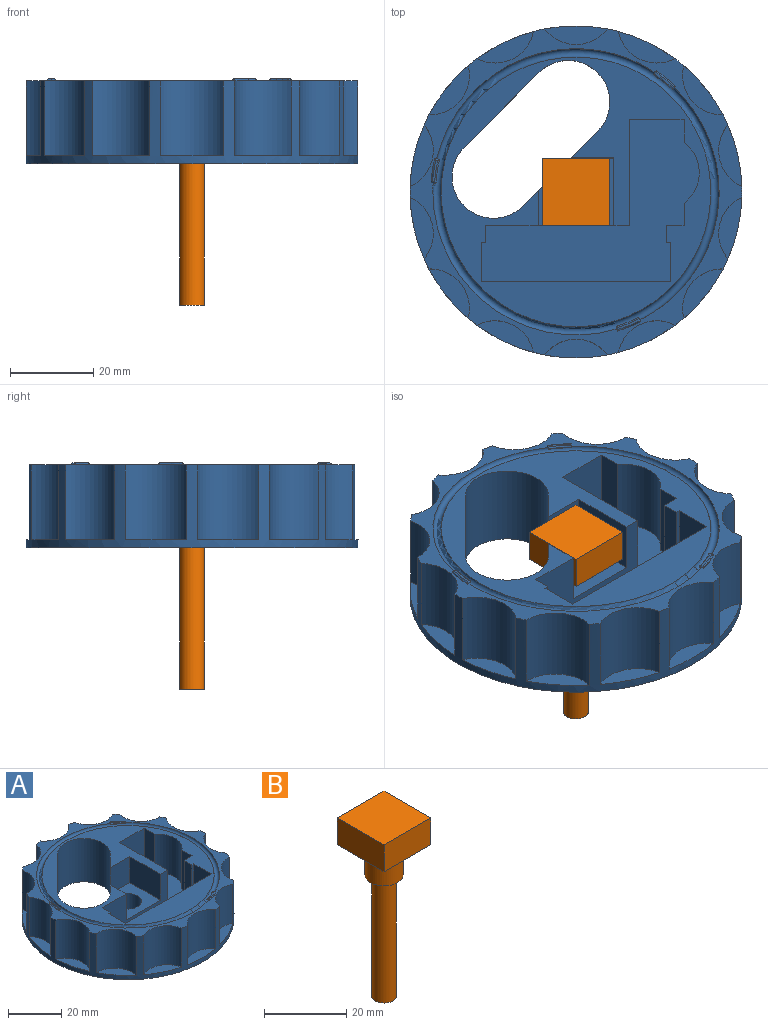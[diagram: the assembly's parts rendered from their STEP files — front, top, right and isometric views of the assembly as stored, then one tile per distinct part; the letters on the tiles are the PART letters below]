
ASSEMBLY  parts=2 mates=1
PART A: 87 faces, bbox 80x80x20.7 mm
  f0: plane 80x78.55mm, normal (0,0,1), area 615.7mm2, adj f17,f19,f20,f21,f22,f23,f24,f25
  f1: plane 65x65mm, normal (0,0,1), area 1245.3mm2, adj f2,f33,f34,f35,f36,f38,f39,f40
  f2: plane 34.78x18mm, normal (0,-1,0), area 407.1mm2, adj f1,f38,f40,f41,f42,f49,f54
  f3: plane 13.66x7.63mm, normal (0,0,1), area 47.3mm2, adj f17,f19
  f4: plane 11.86x9.75mm, normal (0,0,1), area 47.3mm2, adj f17,f32
  f5: plane 14.78x5.61mm, normal (0,0,1), area 47.3mm2, adj f17,f31
  f6: plane 14.78x5.61mm, normal (0,0,1), area 47.3mm2, adj f17,f30
  f7: plane 11.86x9.75mm, normal (0,0,1), area 47.3mm2, adj f17,f29
  f8: plane 13.66x7.63mm, normal (0,0,1), area 47.3mm2, adj f17,f28
  f9: plane 15.16x4.5mm, normal (0,0,1), area 47.3mm2, adj f17,f27
  f10: plane 13.66x7.63mm, normal (0,0,1), area 47.3mm2, adj f17,f26
  f11: plane 11.86x9.75mm, normal (0,0,1), area 47.3mm2, adj f17,f25
  f12: plane 14.78x5.61mm, normal (0,0,1), area 47.3mm2, adj f17,f24
  f13: plane 14.78x5.61mm, normal (0,0,1), area 47.3mm2, adj f17,f23
  f14: plane 11.86x9.75mm, normal (0,0,1), area 47.3mm2, adj f17,f22
  f15: plane 13.66x7.63mm, normal (0,0,1), area 47.3mm2, adj f17,f21
  f16: plane 15.16x4.5mm, normal (0,0,1), area 47.3mm2, adj f17,f20
  f17: cylinder r=40mm len=80mm, axis (0,0,1), area 1182.4mm2, adj f0,f3,f4,f5,f6,f7,f8,f9
  f18: plane 80x80mm, normal (0,0,-1), area 4120.7mm2, adj f17,f33,f34,f35,f36,f37
  f19: cylinder r=9.5mm len=18mm, axis (0,0,-1), area 316mm2, adj f0,f3,f17
  f20: cylinder r=9.5mm len=18mm, axis (0,0,-1), area 316mm2, adj f0,f16,f17
  f21: cylinder r=9.5mm len=18mm, axis (0,0,-1), area 316mm2, adj f0,f15,f17
  f22: cylinder r=9.5mm len=18mm, axis (0,0,-1), area 316mm2, adj f0,f14,f17
  f23: cylinder r=9.5mm len=18mm, axis (0,0,-1), area 316mm2, adj f0,f13,f17
  f24: cylinder r=9.5mm len=18mm, axis (0,0,-1), area 316mm2, adj f0,f12,f17
  f25: cylinder r=9.5mm len=18mm, axis (0,0,-1), area 316mm2, adj f0,f11,f17
  f26: cylinder r=9.5mm len=18mm, axis (0,0,-1), area 316mm2, adj f0,f10,f17
  f27: cylinder r=9.5mm len=18mm, axis (0,0,-1), area 316mm2, adj f0,f9,f17
  f28: cylinder r=9.5mm len=18mm, axis (0,0,-1), area 316mm2, adj f0,f8,f17
  f29: cylinder r=9.5mm len=18mm, axis (0,0,-1), area 316mm2, adj f0,f7,f17
  f30: cylinder r=9.5mm len=18mm, axis (0,0,-1), area 316mm2, adj f0,f6,f17
  f31: cylinder r=9.5mm len=18mm, axis (0,0,-1), area 316mm2, adj f0,f5,f17
  f32: cylinder r=9.5mm len=18mm, axis (0,0,-1), area 316mm2, adj f0,f4,f17
  f33: cylinder r=10mm len=20mm, axis (0,0,1), area 628.3mm2, adj f1,f18,f34,f36
  f34: plane 20x18.03mm, normal (-0.71,0.71,0), area 375.4mm2, adj f1,f18,f33,f35,f39,f40,f41
  f35: cylinder r=10mm len=20mm, axis (0,0,1), area 628.3mm2, adj f1,f18,f34,f36
  f36: plane 20x18.03mm, normal (0.71,-0.71,0), area 510mm2, adj f1,f18,f33,f35
  f37: cylinder r=5.1mm len=10.2mm, axis (0,0,1), area 256.4mm2, adj f18,f41
  f38: plane 16.35x12mm, normal (-1,0,0), area 196.2mm2, adj f1,f2,f39,f41
  f39: plane 12x10.32mm, normal (0,-1,0), area 123.8mm2, adj f1,f34,f38,f41
  f40: plane 12x8.42mm, normal (1,0,0), area 101mm2, adj f1,f2,f34,f41
  f41: plane 18.25x16.35mm, normal (0,0,1), area 185.2mm2, adj f2,f34,f37,f38,f39,f40
  f42: plane 18x4.1mm, normal (1,0,0), area 73.8mm2, adj f1,f2,f43,f49
  f43: plane 18x1mm, normal (0,-1,0), area 18mm2, adj f1,f42,f44,f49
  f44: plane 18x9.4mm, normal (1,0,0), area 169.2mm2, adj f1,f43,f45,f49
  f45: plane 45.7x18mm, normal (0,1,0), area 822.6mm2, adj f1,f44,f46,f49
  f46: plane 18x9.4mm, normal (-1,0,0), area 169.2mm2, adj f1,f45,f47,f49
  f47: plane 18x1mm, normal (0,-1,0), area 18mm2, adj f1,f46,f48,f49
  f48: plane 18x4.1mm, normal (-1,0,0), area 73.8mm2, adj f1,f47,f49,f55
  f49: plane 52.57x39.1mm, normal (0,0,1), area 981.9mm2, adj f2,f42,f43,f44,f45,f46,f47,f48
  f50: plane 18x5.48mm, normal (-1,0,0), area 98.7mm2, adj f1,f49,f51,f55
  f51: cylinder r=9.1mm len=18mm, axis (0,0,1), area 306.1mm2, adj f1,f49,f50,f52
  f52: plane 18x5.48mm, normal (-1,0,0), area 98.7mm2, adj f1,f49,f51,f53
  f53: plane 18x13.1mm, normal (0,-1,0), area 235.8mm2, adj f1,f49,f52,f54
  f54: plane 25.6x18mm, normal (1,0,0), area 460.8mm2, adj f1,f2,f49,f53
  f55: plane 18x4.18mm, normal (0,1,0), area 75.3mm2, adj f1,f48,f49,f50
  f56: torus R=33.5mm, axis (0,0,-1), area 661.3mm2, adj f0,f1,f62,f68,f74
  f57: plane 1x0.66mm, normal (-0.83,0.55,0), area 0.2mm2, adj f0,f58,f60,f62,f84
  f58: cylinder r=33.8mm len=4.52mm, axis (0,0,-1), area 0.9mm2, adj f57,f59,f62,f86
  f59: plane 0.87x0.82mm, normal (0.73,-0.69,0), area 0.2mm2, adj f0,f58,f60,f62,f85
  f60: cylinder r=35mm len=4.68mm, axis (0,0,-1), area 0.9mm2, adj f0,f57,f59,f83
  f61: plane 4.36x3.61mm, normal (0,0,1), area 2.6mm2, adj f83,f84,f85,f86
  f62: plane 5x4.17mm, normal (0,0,-1), area 4.1mm2, adj f56,f57,f58,f59
  f63: plane 1.2x0.15mm, normal (-0.06,-1,0), area 0.2mm2, adj f0,f64,f66,f68,f79
  f64: cylinder r=33.8mm len=5.7mm, axis (0,0,-1), area 0.9mm2, adj f63,f65,f68,f80
  f65: plane 1.17x0.28mm, normal (0.23,0.97,0), area 0.2mm2, adj f0,f64,f66,f68,f82
  f66: cylinder r=35mm len=5.91mm, axis (0,0,-1), area 0.9mm2, adj f0,f63,f65,f81
  f67: plane 5.19x1.25mm, normal (0,0,1), area 2.6mm2, adj f79,f80,f81,f82
  f68: plane 5.87x1.55mm, normal (0,0,-1), area 4.1mm2, adj f56,f63,f64,f65
  f69: plane 1.07x0.53mm, normal (0.9,0.45,0), area 0.2mm2, adj f0,f70,f72,f74,f76
  f70: cylinder r=33.8mm len=5.36mm, axis (0,0,-1), area 0.9mm2, adj f69,f71,f74,f78
  f71: plane 1.15x0.34mm, normal (-0.96,-0.29,0), area 0.2mm2, adj f0,f70,f72,f74,f77
  f72: cylinder r=35mm len=5.55mm, axis (0,0,-1), area 0.9mm2, adj f0,f69,f71,f75
  f73: plane 4.99x2.36mm, normal (0,0,1), area 2.6mm2, adj f75,f76,f77,f78
  f74: plane 5.68x2.79mm, normal (0,0,-1), area 4.1mm2, adj f56,f69,f70,f71
  f75: torus R=34.65mm, axis (0,0,1), area 3.1mm2, adj f72,f73,f76,f77
  f76: cylinder r=0.35mm len=1.23mm, axis (0.45,-0.9,0), area 0.5mm2, adj f69,f73,f75,f78
  f77: cylinder r=0.35mm len=1.25mm, axis (-0.29,0.96,0), area 0.5mm2, adj f71,f73,f75,f78
  f78: torus R=34.15mm, axis (0,0,1), area 3mm2, adj f70,f73,f76,f77
  f79: cylinder r=0.35mm len=1.22mm, axis (-1,0.06,0), area 0.5mm2, adj f63,f67,f80,f81
  f80: torus R=34.15mm, axis (0,0,1), area 3mm2, adj f64,f67,f79,f82
  f81: torus R=34.65mm, axis (0,0,1), area 3.1mm2, adj f66,f67,f79,f82
  f82: cylinder r=0.35mm len=1.25mm, axis (0.97,-0.23,0), area 0.5mm2, adj f65,f67,f80,f81
  f83: torus R=34.65mm, axis (0,0,1), area 3.1mm2, adj f60,f61,f84,f85
  f84: cylinder r=0.35mm len=1.19mm, axis (0.55,0.83,0), area 0.5mm2, adj f57,f61,f83,f86
  f85: cylinder r=0.35mm len=1.11mm, axis (-0.69,-0.73,0), area 0.5mm2, adj f59,f61,f83,f86
  f86: torus R=34.15mm, axis (0,0,1), area 3mm2, adj f58,f61,f84,f85
PART B: 10 faces, bbox 16x16x53 mm
  f0: plane 16x8mm, normal (0,-1,0), area 128mm2, adj f1,f3,f4,f5
  f1: plane 16x8mm, normal (1,0,0), area 128mm2, adj f0,f2,f4,f5
  f2: plane 16x8mm, normal (0,1,0), area 128mm2, adj f1,f3,f4,f5
  f3: plane 16x8mm, normal (-1,0,0), area 128mm2, adj f0,f2,f4,f5
  f4: plane 16x16mm, normal (0,0,1), area 256mm2, adj f0,f1,f2,f3
  f5: plane 16x16mm, normal (0,0,-1), area 188.8mm2, adj f0,f1,f2,f3,f6
  f6: cylinder r=4.62mm len=9.25mm, axis (0,0,1), area 261.5mm2, adj f5,f7
  f7: plane 9.25x9.25mm, normal (0,0,-1), area 38.9mm2, adj f6,f8
  f8: cylinder r=3mm len=36mm, axis (0,0,1), area 678.6mm2, adj f7,f9
  f9: plane 6x6mm, normal (0,0,-1), area 28.3mm2, adj f8
PLACE A t=(-3.03,-2.89,16.79)mm fixed
PLACE B t=(-3.03,-2.89,25.77)mm
MATE slider A.f17 <-> B.f6  axis (0,0,1) through (-3.03,-2.89,14.79)mm
